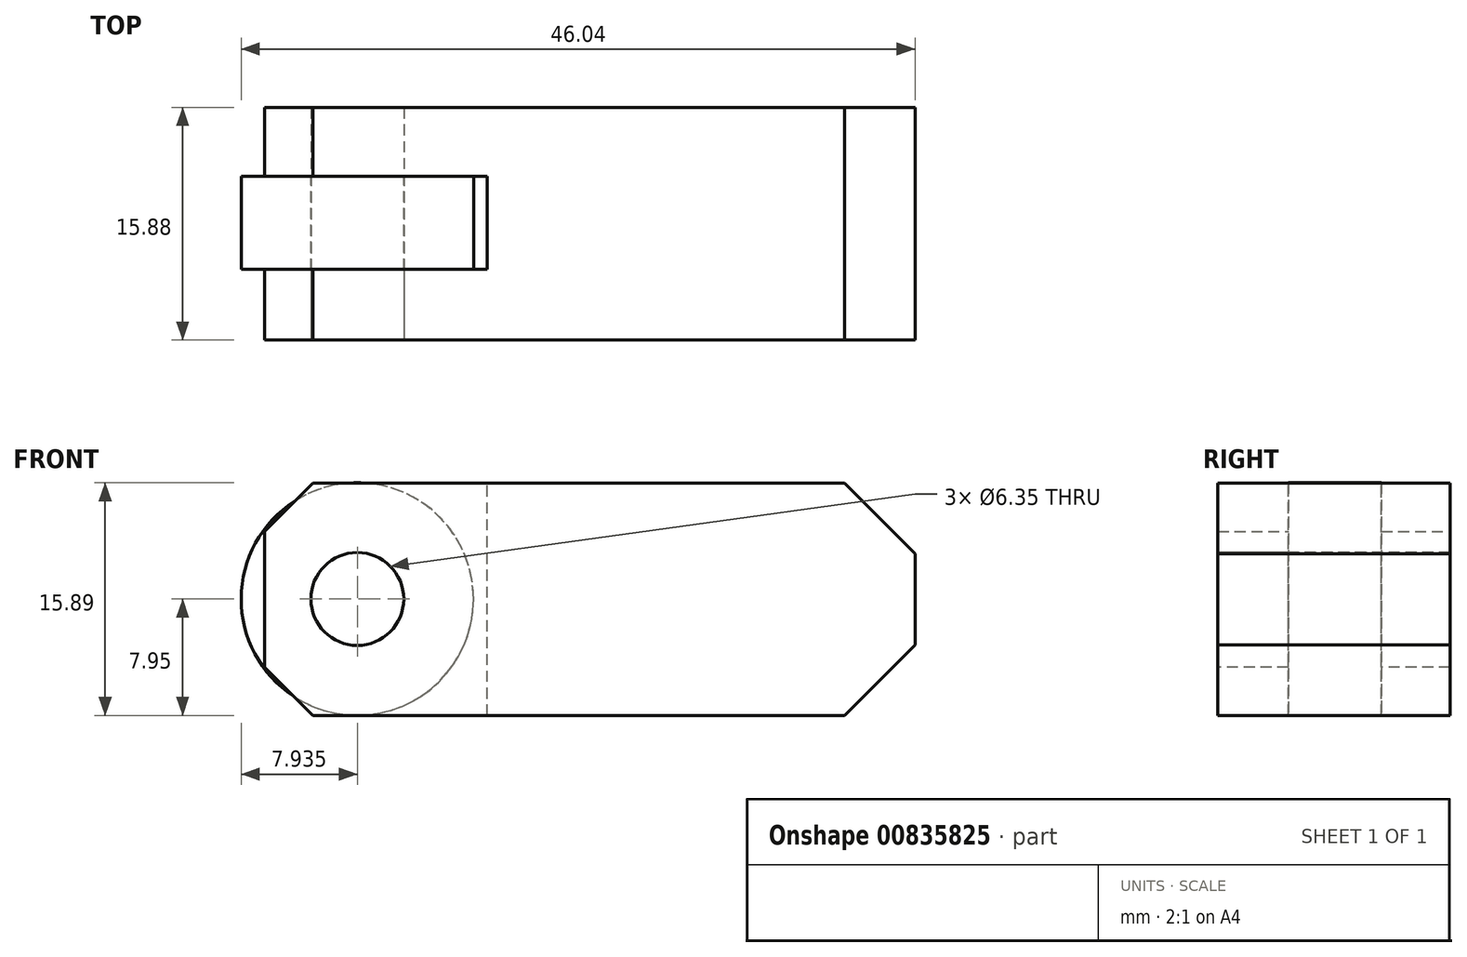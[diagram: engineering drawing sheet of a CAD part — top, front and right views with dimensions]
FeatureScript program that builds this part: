
annotation { "Feature Type Name" : "Feature", "Feature Type Description" : "" }
export const myFeature = defineFeature(function(context is Context, id is Id, definition is map)
    precondition{}
    {
        {
            var Q0;
            Q0=qCreatedBy(makeId("Top.planeOp"),FACE);
            var sketch = newSketch(context, id + "F0", { "sketchPlane" : qUnion([Q0])});
            skLineSegment(sketch, "E0.bottom", {"start": v(22.23, -7.94) * mm, "end": v(-22.23, -7.94) * mm});
            skLineSegment(sketch, "E0.top", {"start": v(22.23, 7.94) * mm, "end": v(-22.23, 7.94) * mm});
            skLineSegment(sketch, "E0.left", {"start": v(22.23, -7.94) * mm, "end": v(22.23, 7.94) * mm});
            skLineSegment(sketch, "E0.right", {"start": v(-22.23, -7.94) * mm, "end": v(-22.23, 7.94) * mm});
            skPoint(sketch, "E0.middle", {"position": v(0, 0) * mm});
            skSolve(sketch);
        }
        {
            var Q0;
            Q0 = qSketchRegion(id + "F0", true);
            extrude(context, id + "F1", {"entities" : qUnion([Q0]), "depth" : 15.88 * mm, "offsetDistance" : 25.4 * mm});
        }
        {
            var Q0;
            Q0=makeQuery(id+"F1.opExtrude","CAP_FACE",FACE,{"disambiguationData":[OSD([sQuery(id+"F0.wireOp",EDGE,"E0.bottom"),sQuery(id+"F0.wireOp",EDGE,"E0.top"),sQuery(id+"F0.wireOp",EDGE,"E0.left"),sQuery(id+"F0.wireOp",EDGE,"E0.right")])],"isStart":false});
            var sketch = newSketch(context, id + "F2", { "sketchPlane" : qUnion([Q0])});
            skLineSegment(sketch, "E1.bottom", {"start": v(-22.23, 3.24) * mm, "end": v(-6.99, 3.24) * mm});
            skLineSegment(sketch, "E1.top", {"start": v(-22.23, -3.11) * mm, "end": v(-6.99, -3.11) * mm});
            skLineSegment(sketch, "E1.left", {"start": v(-22.23, 3.24) * mm, "end": v(-22.23, -3.11) * mm});
            skLineSegment(sketch, "E1.right", {"start": v(-6.99, 3.24) * mm, "end": v(-6.99, -3.11) * mm});
            skSolve(sketch);
        }
        {
            var Q0;
            Q0=makeQuery(id+"F2.imprint","IMPRINT",FACE,{"disambiguationData":[TD([[makeQuery(id+"F2.imprint","IMPRINT",EDGE,{"derivedFrom":sQuery(id+"F2.wireOp",EDGE,"E1.bottom")}),-1.0]])]});
            extrude(context, id + "F3", {"entities" : qUnion([Q0]), "operationType" : NewBodyOperationType.REMOVE, "endBound" : BoundingType.THROUGH_ALL, "oppositeDirection" : true, "depth" : 25.4 * mm, "offsetDistance" : 25.4 * mm});
        }
        {
            var Q0;
            Q0=makeQuery(id+"F1.opExtrude","SWEPT_FACE",FACE,{"disambiguationData":[OSD([sQuery(id+"F0.wireOp",EDGE,"E0.bottom")])]});
            var sketch = newSketch(context, id + "F4", { "sketchPlane" : qUnion([Q0])});
            skCircle(sketch, "E2", {"center": v(-15.88, 7.95) * mm, "radius": 3.18 * mm});
            skSolve(sketch);
        }
        {
            var Q0;
            Q0=makeQuery(id+"F4.imprint","IMPRINT",FACE,{"disambiguationData":[TD([[makeQuery(id+"F4.imprint","IMPRINT",EDGE,{"derivedFrom":sQuery(id+"F4.wireOp",EDGE,"E2")}),1.0]])]});
            extrude(context, id + "F5", {"entities" : qUnion([Q0]), "operationType" : NewBodyOperationType.REMOVE, "endBound" : BoundingType.THROUGH_ALL, "oppositeDirection" : true, "depth" : 25.4 * mm, "offsetDistance" : 25.4 * mm});
        }
        {
            var Q0;
            {var subQ0=sQuery(id+"F0.wireOp",EDGE,"E0.right");var subQ1=sQuery(id+"F0.wireOp",EDGE,"E0.top");Q0=makeQuery(id+"F3.boolean.opBoolean","SPLIT",EDGE,{"disambiguationData":[TD([makeQuery(id+"F1.opExtrude","SWEPT_FACE",FACE,{"disambiguationData":[OSD([subQ1])]})])],"derivedFrom":makeQuery(id+"F1.opExtrude","CAP_EDGE",EDGE,{"disambiguationData":[OSD([subQ0])],"isStart":false})});}
            var Q1;
            {var subQ0=sQuery(id+"F0.wireOp",EDGE,"E0.bottom");var subQ1=sQuery(id+"F0.wireOp",EDGE,"E0.right");Q1=makeQuery(id+"F3.boolean.opBoolean","SPLIT",EDGE,{"disambiguationData":[TD([makeQuery(id+"F1.opExtrude","SWEPT_FACE",FACE,{"disambiguationData":[OSD([subQ0])]})])],"derivedFrom":makeQuery(id+"F1.opExtrude","CAP_EDGE",EDGE,{"disambiguationData":[OSD([subQ1])],"isStart":false})});}
            var Q2;
            {var subQ0=sQuery(id+"F0.wireOp",EDGE,"E0.bottom");var subQ1=sQuery(id+"F0.wireOp",EDGE,"E0.right");Q2=makeQuery(id+"F3.boolean.opBoolean","SPLIT",EDGE,{"disambiguationData":[TD([makeQuery(id+"F1.opExtrude","SWEPT_FACE",FACE,{"disambiguationData":[OSD([subQ0])]})])],"derivedFrom":makeQuery(id+"F1.opExtrude","CAP_EDGE",EDGE,{"disambiguationData":[OSD([subQ1])],"isStart":true})});}
            var Q3;
            {var subQ0=sQuery(id+"F0.wireOp",EDGE,"E0.right");var subQ1=sQuery(id+"F0.wireOp",EDGE,"E0.top");Q3=makeQuery(id+"F3.boolean.opBoolean","SPLIT",EDGE,{"disambiguationData":[TD([makeQuery(id+"F1.opExtrude","SWEPT_FACE",FACE,{"disambiguationData":[OSD([subQ1])]})])],"derivedFrom":makeQuery(id+"F1.opExtrude","CAP_EDGE",EDGE,{"disambiguationData":[OSD([subQ0])],"isStart":true})});}
            chamfer(context, id + "F6", {"entities" : qUnion([Q0, Q1, Q2, Q3]), "width" : 3.3 * mm, "tangentPropagation" : true});
        }
        {
            var Q0;
            Q0=makeQuery(id+"F1.opExtrude","CAP_EDGE",EDGE,{"disambiguationData":[OSD([sQuery(id+"F0.wireOp",EDGE,"E0.left")])],"isStart":false});
            var Q1;
            Q1=makeQuery(id+"F1.opExtrude","CAP_EDGE",EDGE,{"disambiguationData":[OSD([sQuery(id+"F0.wireOp",EDGE,"E0.left")])],"isStart":true});
            chamfer(context, id + "F7", {"entities" : qUnion([Q0, Q1]), "width" : 4.83 * mm, "tangentPropagation" : true});
        }
        {
            var Q0;
            Q0=makeQuery(id+"F1.opExtrude","SWEPT_FACE",FACE,{"disambiguationData":[OSD([sQuery(id+"F0.wireOp",EDGE,"E0.bottom")])]});
            var sketch = newSketch(context, id + "F8", { "sketchPlane" : qUnion([Q0])});
            skCircle(sketch, "E3", {"center": v(-15.88, 7.95) * mm, "radius": 3.18 * mm});
            skSolve(sketch);
        }
        {
            var Q0;
            Q0=makeQuery(id+"F8.imprint","IMPRINT",FACE,{"disambiguationData":[TD([[makeQuery(id+"F8.imprint","IMPRINT",EDGE,{"derivedFrom":sQuery(id+"F8.wireOp",EDGE,"E3")}),1.0]])]});
            extrude(context, id + "F9", {"entities" : qUnion([Q0]), "oppositeDirection" : true, "depth" : 15.88 * mm, "offsetDistance" : 25.4 * mm});
        }
        {
            var Q0;
            Q0=makeQuery(id+"F3.boolean.opBoolean","COPY",FACE,{"derivedFrom":makeQuery(id+"F3.opExtrude","SWEPT_FACE",FACE,{"disambiguationData":[OSD([sQuery(id+"F2.wireOp",EDGE,"E1.bottom")])]})});
            var sketch = newSketch(context, id + "F10", { "sketchPlane" : qUnion([Q0])});
            skCircle(sketch, "E4", {"center": v(-15.87, 7.95) * mm, "radius": 7.94 * mm});
            skCircle(sketch, "E5", {"center": v(-15.87, 7.95) * mm, "radius": 3.18 * mm});
            skSolve(sketch);
        }
        {
            var Q0;
            {var subQ1=sQuery(id+"F2.wireOp",EDGE,"E1.bottom");var subQ4=sQuery(id+"F0.wireOp",EDGE,"E0.right");var subQ14=makeQuery(id+"F3.boolean.opBoolean","COPY",EDGE,{"derivedFrom":makeQuery(id+"F3.opExtrude","SWEPT_EDGE",EDGE,{"disambiguationData":[OSD([subQ4,subQ1,sQuery(id+"F2.wireOp",EDGE,"E1.left")])]})});Q0=makeQuery(id+"F10.imprint","IMPRINT",FACE,{"disambiguationData":[TD([[makeQuery(id+"F10.imprint","IMPRINT",EDGE,{"derivedFrom":subQ14}),1.0]])]});}
            var Q1;
            Q1=makeQuery(id+"F10.imprint","IMPRINT",FACE,{"disambiguationData":[TD([[makeQuery(id+"F10.imprint","IMPRINT",EDGE,{"derivedFrom":sQuery(id+"F10.wireOp",EDGE,"E5")}),-1.0]])]});
            var Q2;
            {var subQ0=sQuery(id+"F10.wireOp",EDGE,"E4");var subQ1=makeQuery(id+"F3.boolean.opBoolean","COPY",EDGE,{"derivedFrom":makeQuery(id+"F3.opExtrude","CAP_EDGE",EDGE,{"disambiguationData":[OSD([sQuery(id+"F2.wireOp",EDGE,"E1.bottom")])],"isStart":true})});var subQ2=makeQuery(id+"F10.imprint","INTERSECT",VERTEX,{"disambiguationData":[OD(0.0)],"derivedFrom":[subQ1,subQ0]});Q2=makeQuery(id+"F10.imprint","IMPRINT",FACE,{"disambiguationData":[TD([[makeQuery(id+"F10.imprint","IMPRINT",EDGE,{"disambiguationData":[TD([[subQ2,1.0]])],"derivedFrom":subQ0}),1.0]])]});}
            extrude(context, id + "F11", {"entities" : qUnion([Q0, Q1, Q2]), "depth" : 6.35 * mm, "offsetDistance" : 25.4 * mm});
        }
    });
